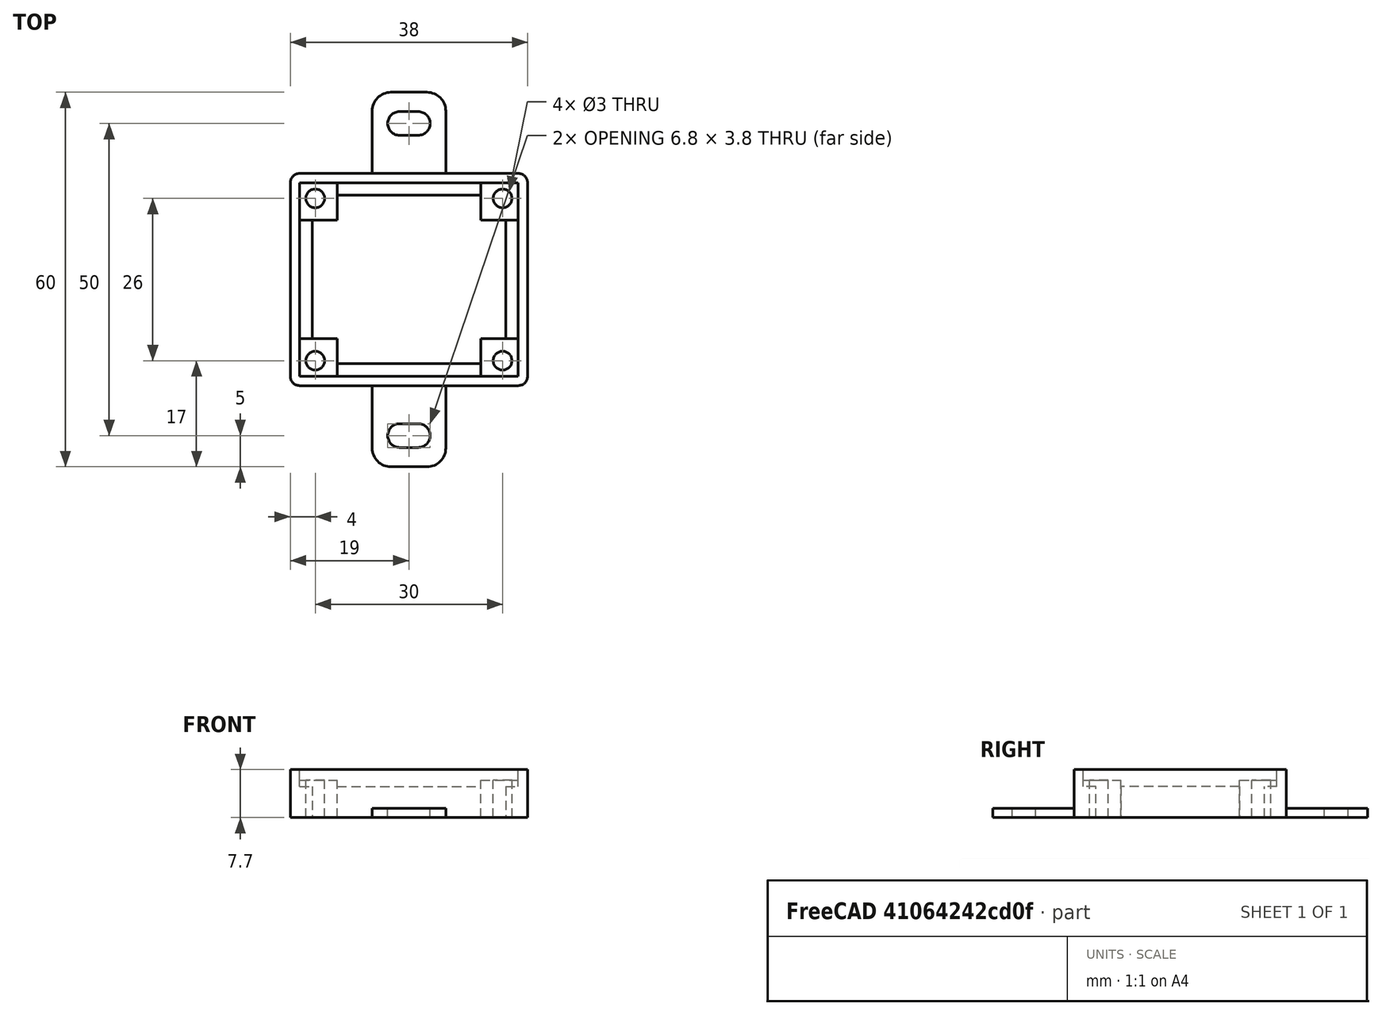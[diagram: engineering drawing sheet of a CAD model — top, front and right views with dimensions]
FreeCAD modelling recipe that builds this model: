
FCSTD DOCUMENT  (FreeCAD 0.19R23578 (Git))
Label: stepper_driver_x113647
License: All rights reserved
LicenseURL: http://en.wikipedia.org/wiki/All_rights_reserved
objects: Part::Box×4, Part::MultiFuse×3, Part::FeaturePython×2, Part::Cut×2, Spreadsheet::Sheet×1, Part::Cylinder×1, Part::Fillet×1, Part::Feature×1, App::Part×1
note: 14 computed .brp shape members not serialized (recipe doc carries the construction recipe); baked Part::Feature solids carry a one-line shape summary decoded from their .brp

FEATURE [Spreadsheet::Sheet] Spreadsheet  label="p"
  cells = A1=hole_x_dist; B1(hole_x_dist)=30; A2=hole_y_dist; B2(hole_y_dist)=26; A3=pcb_under; B3(pcb_under)=3; A4=pcb_x; B4(pcb_x)=35; A5=pcb_y; B5(pcb_y)=31; A6=hole_stand_x; B6(hole_stand_x)=6; A7=hole_stand_y; B7(hole_stand_y)=6; A8=hole_r; B8(hole_r)=1.5; A9=box_wall; B9(box_wall)=1.5; A10=under_layer; B10(under_layer)=3; A11=pcb_height; B11(pcb_height)=1.7; A12=under_pcb_border; B12(under_pcb_border)=2
FEATURE [Part::Box] Box  label="bottom cube"
  AttacherType = Attacher::AttachEngine3D
  Height = 7.7
  Length = 38
  Width = 34
  expr: Height = <<p>>.pcb_under + <<p>>.pcb_height + <<p>>.under_layer
  expr: Length = <<p>>.pcb_x + <<p>>.box_wall * 2
  expr: Width = <<p>>.pcb_y + <<p>>.box_wall * 2
FEATURE [Part::Box] Box001  label="bottom extraction"
  AttacherType = Attacher::AttachEngine3D
  Height = 10
  Length = 31
  Placement = pos=(3.5,3.5,0) rot=(0,0,1;0rad)
  Width = 27
  expr: Width = <<p>>.pcb_y - <<p>>.under_pcb_border * 2
  expr: Length = <<p>>.pcb_x - <<p>>.under_pcb_border * 2
  expr: .Placement.Base.x = <<p>>.under_pcb_border + <<p>>.box_wall
  expr: .Placement.Base.y = <<p>>.under_pcb_border + <<p>>.box_wall
FEATURE [Part::Box] Box002  label="pcb extraction"
  AttacherType = Attacher::AttachEngine3D
  Height = 10
  Length = 35
  Placement = pos=(1.5,1.5,5) rot=(0,0,1;0rad)
  Width = 31
  expr: Width = <<p>>.pcb_y
  expr: Length = <<p>>.pcb_x
  expr: .Placement.Base.x = <<p>>.box_wall
  expr: .Placement.Base.y = <<p>>.box_wall
  expr: .Placement.Base.z = <<p>>.under_pcb_border + <<p>>.under_layer
FEATURE [Part::MultiFuse] Fusion  label="bottom extraction001"
  Shapes = -> [Box001,Box002]
FEATURE [Part::Box] Box003  label="hole stand cube"
  AttacherType = Attacher::AttachEngine3D
  Height = 6
  Length = 6
  Placement = pos=(1.5,1.5,0) rot=(0,0,1;0rad)
  Width = 6
  expr: Length = <<p>>.hole_stand_x
  expr: Width = <<p>>.hole_stand_y
  expr: Height = <<p>>.pcb_under + <<p>>.under_layer
  expr: .Placement.Base.x = <<p>>.box_wall
  expr: .Placement.Base.y = <<p>>.box_wall
FEATURE [Part::FeaturePython] Array  label="hole stand array"  # Draft array (typed FeaturePython)
  Angle = 360
  ArrayType = 0
  Axis = (0,0,1)
  Base = -> Box003
  Center = (0,0,0)
  Fuse = false
  IntervalAxis = (0,0,0)
  IntervalX = (29,0,0)
  IntervalY = (0,25,0)
  IntervalZ = (0,0,1)
  NumberPolar = 1
  NumberX = 2
  NumberY = 2
  NumberZ = 1
  expr: .IntervalX.x = <<p>>.pcb_x - <<p>>.hole_stand_x
  expr: .IntervalY.y = <<p>>.pcb_y - <<p>>.hole_stand_y
FEATURE [Part::Cylinder] Cylinder  label="pcb hole"
  Angle = 360
  AttacherType = Attacher::AttachEngine3D
  Height = 10
  Placement = pos=(4,4,0) rot=(0,0,1;0rad)
  Radius = 1.5
  expr: Radius = <<p>>.hole_r
  expr: .Placement.Base.x = (<<p>>.box_wall * 2 + <<p>>.pcb_x - <<p>>.hole_x_dist) / 2
  expr: .Placement.Base.y = (<<p>>.box_wall * 2 + <<p>>.pcb_y - <<p>>.hole_y_dist) / 2
FEATURE [Part::FeaturePython] Array001  label="hole array"  # Draft array (typed FeaturePython)
  Angle = 360
  ArrayType = 0
  Axis = (0,0,1)
  Base = -> Cylinder
  Center = (0,0,0)
  Fuse = false
  IntervalAxis = (0,0,0)
  IntervalX = (30,0,0)
  IntervalY = (0,26,0)
  IntervalZ = (0,0,1)
  NumberPolar = 1
  NumberX = 2
  NumberY = 2
  NumberZ = 1
  expr: .IntervalX.x = <<p>>.hole_x_dist
  expr: .IntervalY.y = <<p>>.hole_y_dist
FEATURE [Part::Fillet] Fillet001  label="bottom cube fillet"
  Base = -> Box
  Edges = 4 edges r=1.5: [Edge1,Edge3,Edge5,Edge7]
FEATURE [Part::Feature] Cut002002  label="attach plane y dir002"
  Placement = pos=(13.1,-13,0) rot=(0,0,1;0rad)
  shape: bbox 11.8 x 60 x 1.5 mm, 20 faces (baked)
FEATURE [Part::MultiFuse] Fusion002  label="bottom fusion"
  Shapes = -> [Fillet001,Cut002002]
FEATURE [Part::Cut] Cut  label="pcb box cut"
  Base = -> Fusion002
  Tool = -> Fusion
FEATURE [Part::MultiFuse] Fusion001  label="frame fusion"
  Shapes = -> [Array,Cut]
FEATURE [Part::Cut] Cut001  label="frame fusion with holes"
  Base = -> Fusion001
  Tool = -> Array001
FEATURE [App::Part] Part  label="pcb with 4 holes part"
  Group = -> [Fusion,Fusion002,Box002,Box003,Box001,Array001,Cut,Array,Cylinder,Fusion001,Cut001]
  Origin = -> Origin
